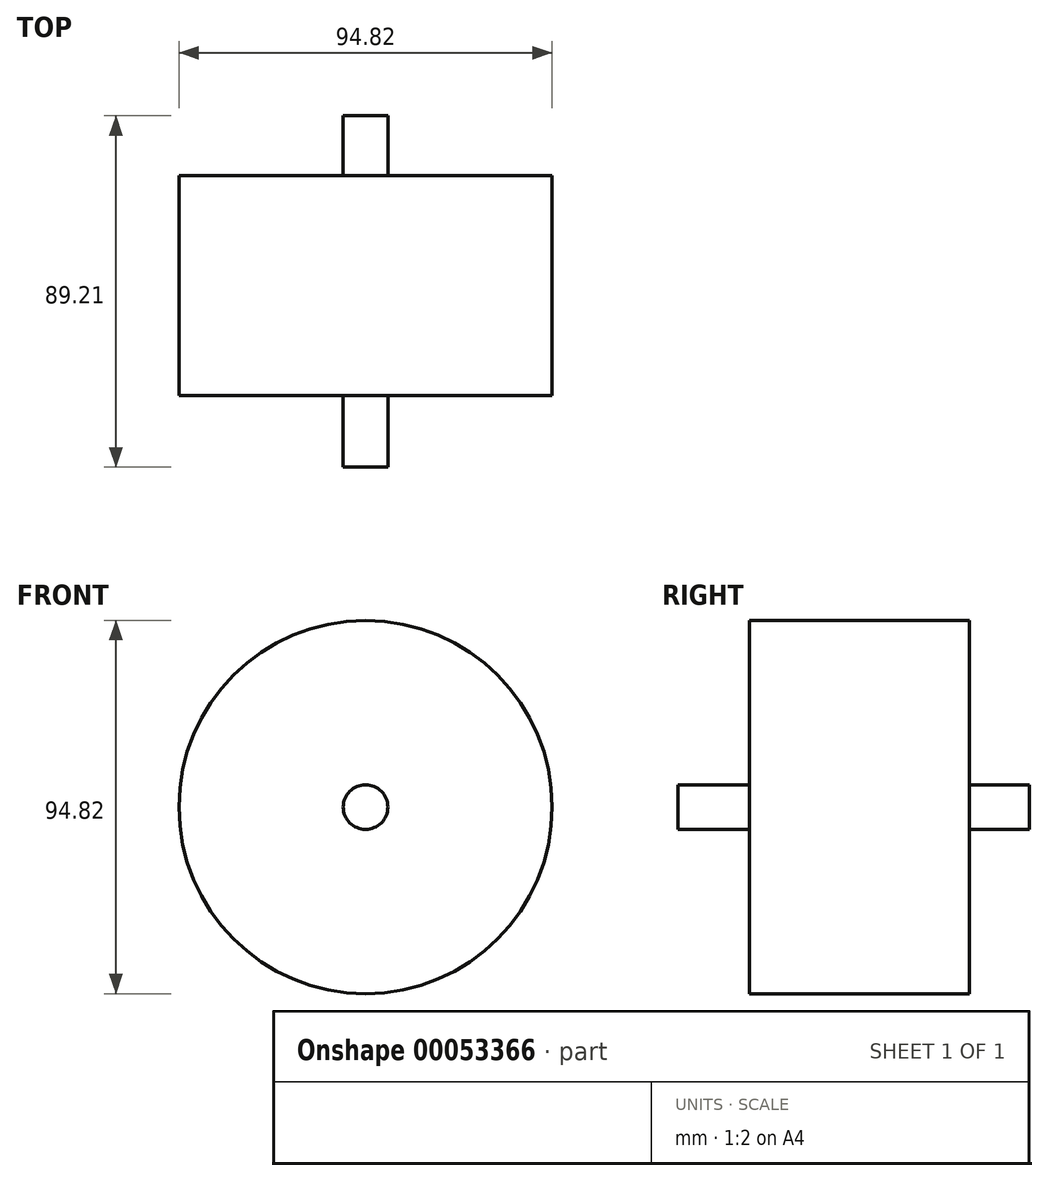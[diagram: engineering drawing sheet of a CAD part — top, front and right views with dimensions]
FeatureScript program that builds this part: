
annotation { "Feature Type Name" : "Feature", "Feature Type Description" : "" }
export const myFeature = defineFeature(function(context is Context, id is Id, definition is map)
    precondition{}
    {
        {
            var Q0;
            Q0=qCreatedBy(makeId("Front.planeOp"),FACE);
            var sketch = newSketch(context, id + "F0", { "sketchPlane" : qUnion([Q0])});
            skLineSegment(sketch, "E0.bottom", {"start": v(-76.14, 76.3) * mm, "end": v(76.19, 76.3) * mm});
            skLineSegment(sketch, "E0.top", {"start": v(-76.14, 0) * mm, "end": v(76.19, 0) * mm});
            skLineSegment(sketch, "E0.left", {"start": v(-76.14, 76.3) * mm, "end": v(-76.14, 0) * mm});
            skLineSegment(sketch, "E0.right", {"start": v(76.19, 76.3) * mm, "end": v(76.19, 0) * mm});
            skSolve(sketch);
        }
        {
            var Q0;
            Q0=makeQuery(id+"F0.imprint","IMPRINT",FACE,{"disambiguationData":[TD([[makeQuery(id+"F0.imprint","IMPRINT",EDGE,{"derivedFrom":sQuery(id+"F0.wireOp",EDGE,"E0.bottom")}),-1.0]])]});
            extrude(context, id + "F1", {"entities" : qUnion([Q0]), "depth" : 44.45 * mm});
        }
        {
            var Q0;
            Q0=makeQuery(id+"F1.opExtrude","SWEPT_FACE",FACE,{"disambiguationData":[OSD([sQuery(id+"F0.wireOp",EDGE,"E0.top")])]});
            shell(context, id + "F2", {"entities" : qUnion([Q0]), "thickness" : 2.54 * mm});
        }
        {
            var Q0;
            Q0=makeQuery(id+"F1.opExtrude","SWEPT_FACE",FACE,{"disambiguationData":[OSD([sQuery(id+"F0.wireOp",EDGE,"E0.left")])]});
            var sketch = newSketch(context, id + "F3", { "sketchPlane" : qUnion([Q0])});
            skLineSegment(sketch, "E1.bottom", {"start": v(15.87, 48.36) * mm, "end": v(34.47, 48.36) * mm});
            skLineSegment(sketch, "E1.top", {"start": v(15.87, 56.54) * mm, "end": v(34.47, 56.54) * mm});
            skLineSegment(sketch, "E1.left", {"start": v(15.87, 48.36) * mm, "end": v(15.87, 56.54) * mm});
            skLineSegment(sketch, "E1.right", {"start": v(34.47, 48.36) * mm, "end": v(34.47, 56.54) * mm});
            skSolve(sketch);
        }
        {
            var Q0;
            Q0=makeQuery(id+"F3.imprint","IMPRINT",FACE,{"disambiguationData":[TD([[makeQuery(id+"F3.imprint","IMPRINT",EDGE,{"derivedFrom":sQuery(id+"F3.wireOp",EDGE,"E1.bottom")}),1.0]])]});
            extrude(context, id + "F4", {"entities" : qUnion([Q0]), "operationType" : NewBodyOperationType.ADD, "depth" : 38.1 * mm});
        }
        {
            var Q0;
            Q0=makeQuery(id+"F4.opExtrude","CAP_FACE",FACE,{"disambiguationData":[OSD([sQuery(id+"F3.wireOp",EDGE,"E1.bottom"),sQuery(id+"F3.wireOp",EDGE,"E1.top"),sQuery(id+"F3.wireOp",EDGE,"E1.left"),sQuery(id+"F3.wireOp",EDGE,"E1.right")])],"isStart":false});
            var Q1;
            Q1=makeQuery(id+"F4.opExtrude","SWEPT_FACE",FACE,{"disambiguationData":[OSD([sQuery(id+"F3.wireOp",EDGE,"E1.top")])]});
            shell(context, id + "F5", {"entities" : qUnion([Q0, Q1]), "thickness" : 2.54 * mm});
        }
        {
            var Q0;
            Q0=makeQuery(id+"F1.opExtrude","SWEPT_BODY",BODY,{"disambiguationData":[OSD([sQuery(id+"F0.wireOp",EDGE,"E0.bottom"),sQuery(id+"F0.wireOp",EDGE,"E0.top"),sQuery(id+"F0.wireOp",EDGE,"E0.left"),sQuery(id+"F0.wireOp",EDGE,"E0.right")])]});
            deleteBodies(context, id + "F6", {"entities" : qUnion([Q0])});
        }
        {
            var Q0;
            Q0=qCreatedBy(makeId("Front.planeOp"),FACE);
            var sketch = newSketch(context, id + "F7", { "sketchPlane" : qUnion([Q0])});
            skCircle(sketch, "E2", {"center": v(0, 0) * mm, "radius": 5.67 * mm});
            skSolve(sketch);
        }
        {
            var Q0;
            Q0=makeQuery(id+"F7.imprint","IMPRINT",FACE,{"disambiguationData":[TD([[makeQuery(id+"F7.imprint","IMPRINT",EDGE,{"derivedFrom":sQuery(id+"F7.wireOp",EDGE,"E2")}),1.0]])]});
            extrude(context, id + "F8", {"entities" : qUnion([Q0]), "depth" : 89.2 * mm});
        }
        {
            var Q0;
            Q0=qCreatedBy(makeId("Right.planeOp"),FACE);
            var sketch = newSketch(context, id + "F9", { "sketchPlane" : qUnion([Q0])});
            skLineSegment(sketch, "E3", {"start": v(-71.09, 0) * mm, "end": v(-71.09, 47.41) * mm});
            skLineSegment(sketch, "E4", {"start": v(-71.09, 47.41) * mm, "end": v(-15.17, 47.41) * mm});
            skLineSegment(sketch, "E5", {"start": v(-15.17, 47.41) * mm, "end": v(-15.17, 0) * mm});
            skLineSegment(sketch, "E6", {"start": v(-15.17, 0) * mm, "end": v(-71.09, 0) * mm});
            skSolve(sketch);
        }
        {
            var Q0;
            Q0=makeQuery(id+"F9.imprint","IMPRINT",FACE,{"disambiguationData":[TD([[makeQuery(id+"F9.imprint","IMPRINT",EDGE,{"derivedFrom":sQuery(id+"F9.wireOp",EDGE,"E3")}),-1.0]])]});
            var Q1;
            Q1=sQuery(id+"F9.wireOp",EDGE,"E6");
            revolve(context, id + "F10", {"operationType" : NewBodyOperationType.ADD, "entities" : qUnion([Q0]), "axis" : qUnion([Q1]), "revolveType" : RevolveType.FULL});
        }
    });
